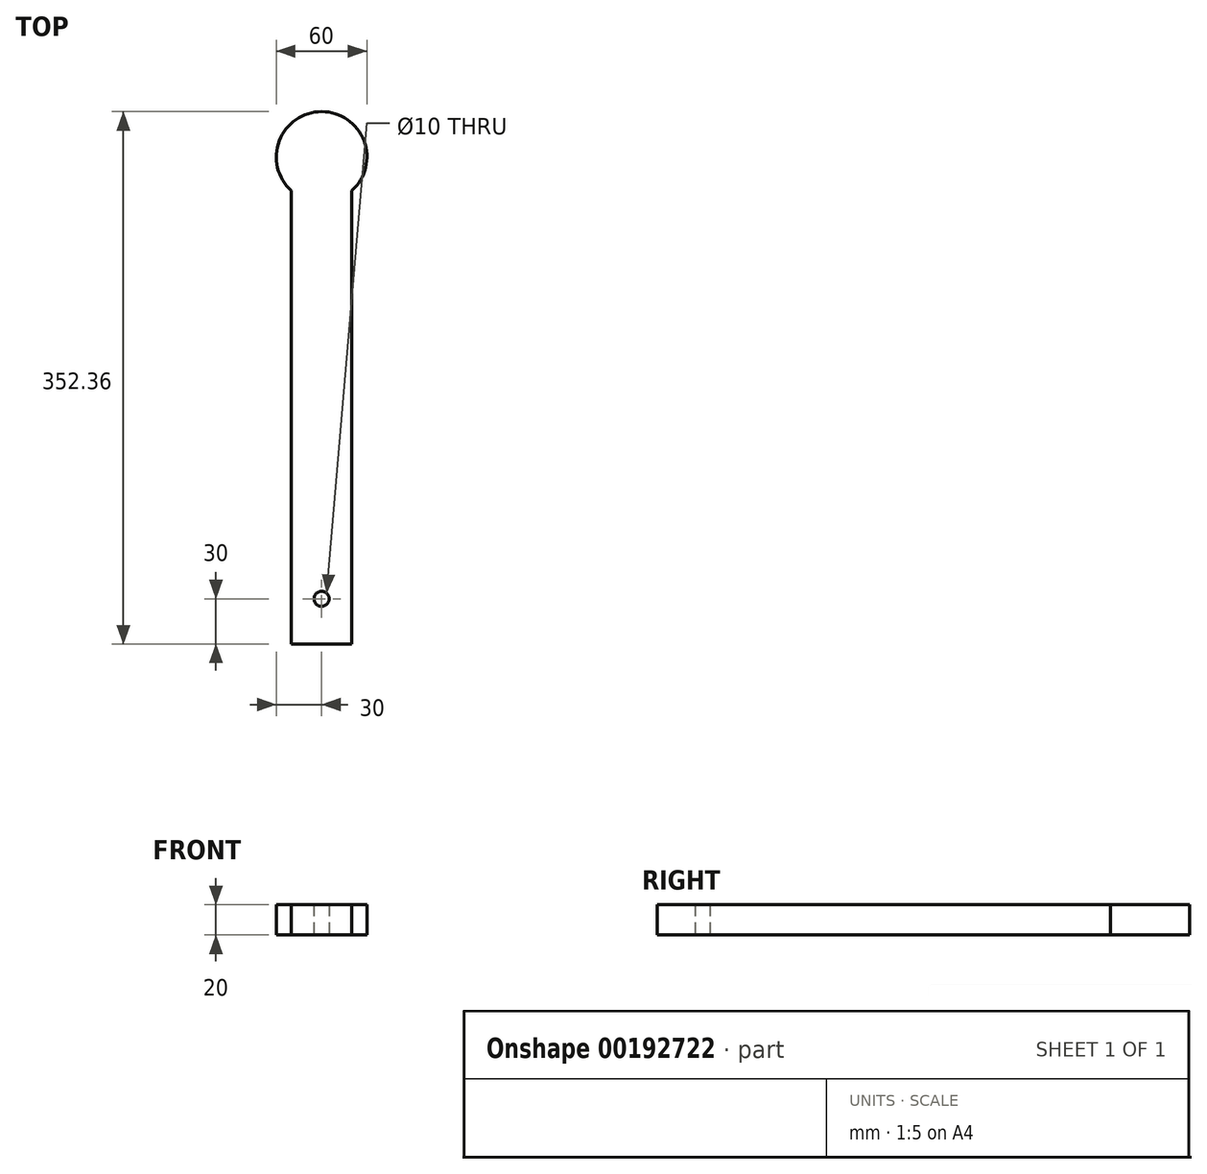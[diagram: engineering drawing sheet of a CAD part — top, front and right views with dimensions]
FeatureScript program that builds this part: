
annotation { "Feature Type Name" : "Feature", "Feature Type Description" : "" }
export const myFeature = defineFeature(function(context is Context, id is Id, definition is map)
    precondition{}
    {
        {
            var Q0;
            Q0=qCreatedBy(makeId("Top.planeOp"),FACE);
            var sketch = newSketch(context, id + "F0", { "sketchPlane" : qUnion([Q0])});
            skLineSegment(sketch, "E0", {"start": v(0, 0) * mm, "end": v(20, 0) * mm});
            skLineSegment(sketch, "E1", {"start": v(20, 0) * mm, "end": v(20, 300) * mm});
            skLineSegment(sketch, "E2", {"start": v(0, 0) * mm, "end": v(0, 38.4) * mm, "construction": true});
            skLineSegment(sketch, "E3.MirrorCS", {"start": v(0, 0) * mm, "end": v(-20, 0) * mm});
            skLineSegment(sketch, "E4.MirrorCS", {"start": v(-20, 0) * mm, "end": v(-20, 300) * mm});
            skArc(sketch, "E5", {"start": v(20, 300) * mm, "mid": v(0, 352.36) * mm, "end": v(-20, 300) * mm});
            skSolve(sketch);
        }
        {
            var Q0;
            Q0=qSketchRegion(id+"F0",true);
            extrude(context, id + "F1", {"entities" : qUnion([Q0]), "depth" : 20 * mm});
        }
        {
            var Q0;
            Q0=makeQuery(id+"F1.opExtrude","CAP_FACE",FACE,{"disambiguationData":[OSD([sQuery(id+"F0.wireOp",EDGE,"E0"),sQuery(id+"F0.wireOp",EDGE,"E1"),sQuery(id+"F0.wireOp",EDGE,"E3.MirrorCS"),sQuery(id+"F0.wireOp",EDGE,"E4.MirrorCS"),sQuery(id+"F0.wireOp",EDGE,"E5")])],"isStart":true});
            var sketch = newSketch(context, id + "F2", { "sketchPlane" : qUnion([Q0])});
            skLineSegment(sketch, "E6", {"start": v(0, 0) * mm, "end": v(0, -30) * mm, "construction": true});
            skCircle(sketch, "E7", {"center": v(0, -30) * mm, "radius": 5 * mm});
            skSolve(sketch);
        }
        {
            var Q0;
            Q0=qSketchRegion(id+"F2",true);
            extrude(context, id + "F3", {"entities" : qUnion([Q0]), "operationType" : NewBodyOperationType.REMOVE, "endBound" : BoundingType.THROUGH_ALL, "oppositeDirection" : true, "depth" : 25 * mm});
        }
    });
